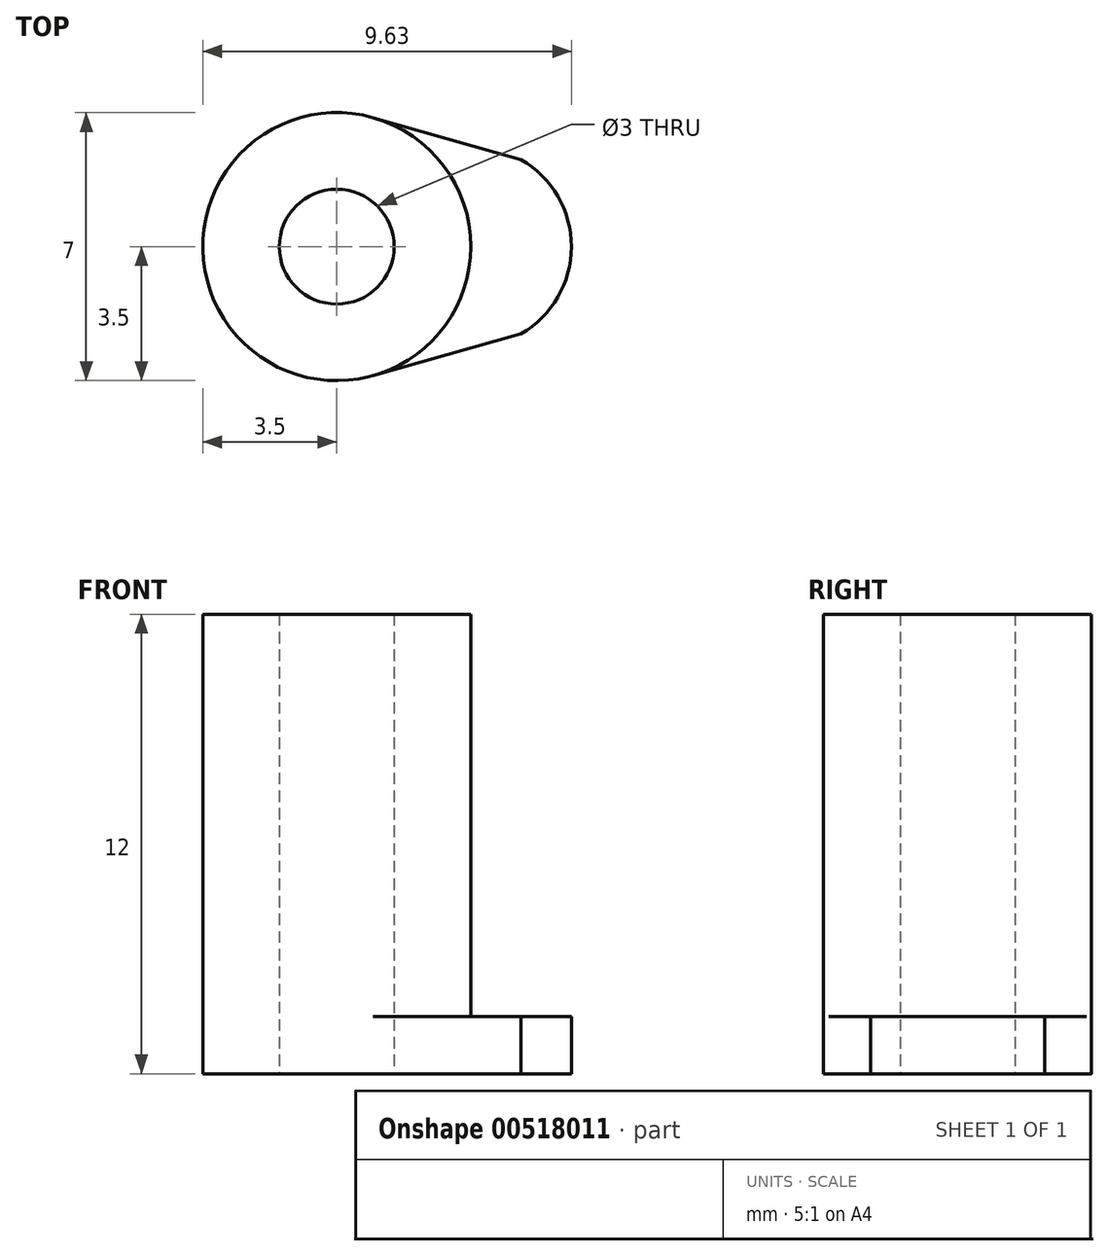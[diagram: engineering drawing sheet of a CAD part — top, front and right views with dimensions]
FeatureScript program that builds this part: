
annotation { "Feature Type Name" : "Feature", "Feature Type Description" : "" }
export const myFeature = defineFeature(function(context is Context, id is Id, definition is map)
    precondition{}
    {
        {
            var Q0;
            Q0=qCreatedBy(makeId("Top.planeOp"),FACE);
            var sketch = newSketch(context, id + "F0", { "sketchPlane" : qUnion([Q0])});
            skCircle(sketch, "E0", {"center": v(0, 0) * mm, "radius": 3.5 * mm});
            skCircle(sketch, "E1", {"center": v(0, 0) * mm, "radius": 1.5 * mm});
            skArc(sketch, "E2", {"start": v(4.81, -2.27) * mm, "mid": v(6.13, 0) * mm, "end": v(4.81, 2.27) * mm});
            skLineSegment(sketch, "E3", {"start": v(4.81, 2.27) * mm, "end": v(0.95, 3.37) * mm});
            skLineSegment(sketch, "E4", {"start": v(4.81, -2.27) * mm, "end": v(0.95, -3.37) * mm});
            skSolve(sketch);
        }
        {
            var Q0;
            Q0=makeQuery(id+"F0.imprint","IMPRINT",FACE,{"disambiguationData":[TD([[makeQuery(id+"F0.imprint","IMPRINT",EDGE,{"derivedFrom":sQuery(id+"F0.wireOp",EDGE,"E1")}),-1.0]])]});
            extrude(context, id + "F1", {"entities" : qUnion([Q0]), "depth" : 12 * mm, "offsetDistance" : 25 * mm});
        }
        {
            var Q0;
            Q0=makeQuery(id+"F0.imprint","IMPRINT",FACE,{"disambiguationData":[TD([[makeQuery(id+"F0.imprint","IMPRINT",EDGE,{"derivedFrom":sQuery(id+"F0.wireOp",EDGE,"E2")}),1.0]])]});
            extrude(context, id + "F2", {"entities" : qUnion([Q0]), "operationType" : NewBodyOperationType.ADD, "depth" : 1.5 * mm, "offsetDistance" : 25 * mm});
        }
    });
